# Revit family: Mounting Brackets PNR-05515
name_source: partatom
category: Generic Models
revit_build: Autodesk Revit 2017 (Build: 20190508_0315(x64)
units: mm (PartAtom-declared; Revit-internal decimal feet)

## family parameters
Always vertical = No
Can host rebar = No
Cut with Voids When Loaded = No
Part Type = Normal
Room Calculation Point = No
Round Connector Dimension = Use Diameter
Shared = No
Work Plane-Based = Yes

## types (6) — shared parameters
Assembly Code = 63.0
Bolt_Material = Brass, Soft Yellow, Welded
Bracket Article Number = *User Defined
Bracket_Width = 15 mm  [stored 0.0492126 ft]
Default Elevation = 1219 mm
Description = Mounting Brackets
Find - Bracket Article Number = https://www.veko.com
Manufacturer = Veko Lightsystems
Mounting_Material = Aluminum 7175 T73 0 Hot Formed
Pendulum Visibility = No

## per-type parameters (varying)
| type | 61-B1-R | B1-R | B7-R | B7SO-R | Bolt_Visibility | Pendulum Start |
| B1-R | No | Yes | No | No | No | 57 mm |
| 61-B1-R | Yes | No | No | No | No | 48 mm |
| B7SO-R | No | No | No | Yes | Yes | 53 mm |
| B7-R | No | No | Yes | No | Yes | 105 mm |
| B2-S-733-R | No | No | No | No | No | 87 mm |
| B2-SO-733-R | No | No | No | No | No | 107 mm |

note: column(s) folded — value = type name in every type: Model

type visibility flags (boolean, named after types; folded from table):
- B1-R: Yes: (none)
- 61-B1-R: Yes: (none)
- B7SO-R: Yes: (none)
- B7-R: Yes: (none)
- B2-S-733-R: Yes: B2-S-733-R
- B2-SO-733-R: Yes: B2-SO-733-R

note: [stored X ft] marks values corroborated as IEEE doubles in the binary element streams (Revit-internal decimal feet)

## geometry (parser evidence)
native form markers: Sweep x2
no freeform markers — native parametric forms only
